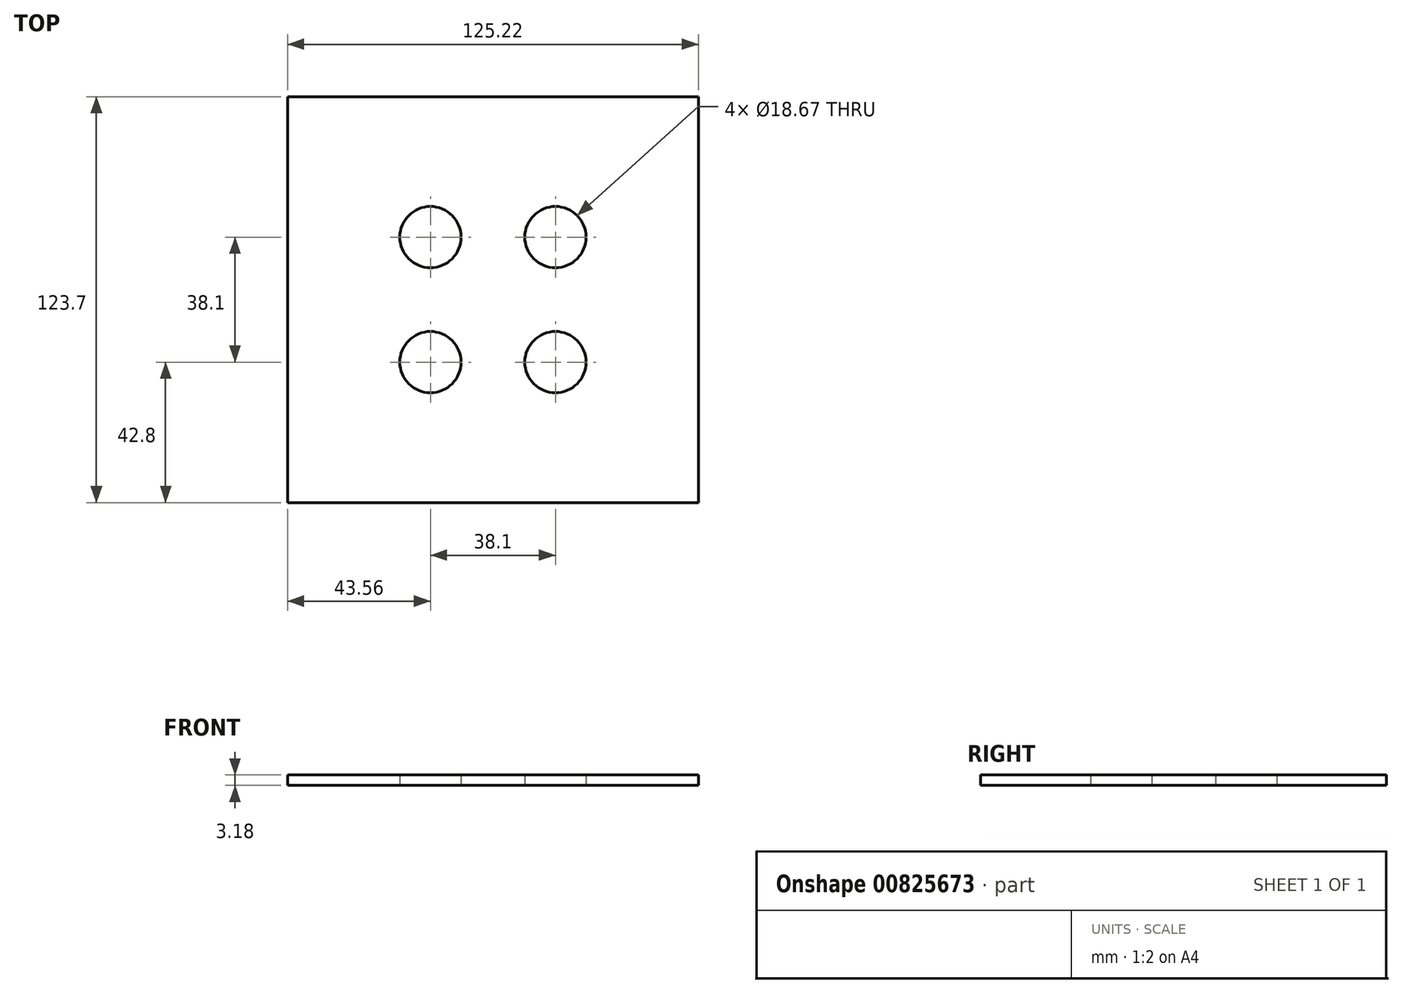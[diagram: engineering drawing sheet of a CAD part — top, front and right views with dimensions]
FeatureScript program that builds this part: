
annotation { "Feature Type Name" : "Feature", "Feature Type Description" : "" }
export const myFeature = defineFeature(function(context is Context, id is Id, definition is map)
    precondition{}
    {
        {
            var Q0;
            Q0=qCreatedBy(makeId("Top.planeOp"),FACE);
            var sketch = newSketch(context, id + "F0", { "sketchPlane" : qUnion([Q0])});
            skLineSegment(sketch, "E0.bottom", {"start": v(-62.61, 61.85) * mm, "end": v(62.61, 61.85) * mm});
            skLineSegment(sketch, "E0.top", {"start": v(-62.61, -61.85) * mm, "end": v(62.61, -61.85) * mm});
            skLineSegment(sketch, "E0.left", {"start": v(-62.61, 61.85) * mm, "end": v(-62.61, -61.85) * mm});
            skLineSegment(sketch, "E0.right", {"start": v(62.61, 61.85) * mm, "end": v(62.61, -61.85) * mm});
            skPoint(sketch, "E0.middle", {"position": v(0, 0) * mm});
            skCircle(sketch, "E1", {"center": v(-19.05, 19.05) * mm, "radius": 9.33 * mm});
            skCircle(sketch, "E2", {"center": v(-19.05, -19.05) * mm, "radius": 9.33 * mm});
            skCircle(sketch, "E3", {"center": v(19.05, 19.05) * mm, "radius": 9.33 * mm});
            skCircle(sketch, "E4", {"center": v(19.05, -19.05) * mm, "radius": 9.33 * mm});
            skSolve(sketch);
        }
        {
            var Q0;
            Q0=makeQuery(id+"F0.imprint","IMPRINT",FACE,{"disambiguationData":[TD([[makeQuery(id+"F0.imprint","IMPRINT",EDGE,{"derivedFrom":sQuery(id+"F0.wireOp",EDGE,"E0.bottom")}),-1.0]])]});
            extrude(context, id + "F1", {"entities" : qUnion([Q0]), "depth" : 3.17 * mm, "offsetDistance" : 25.4 * mm});
        }
    });
